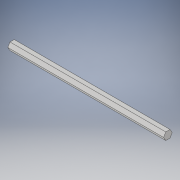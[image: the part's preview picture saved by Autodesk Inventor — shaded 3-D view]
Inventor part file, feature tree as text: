
AUTODESK INVENTOR PART (.ipt)
format: ipt  version: 2018 (Build 220112000, 112)  size: 96,256 bytes
history: native  units: in
note: dims shown in document units (in); Inventor stores cm internally (conversion verified against a paired STEP export)
features: extrude x1, sketch x1
ambient origin geometry x8: Origin, YZ Plane, XZ Plane, XY Plane, X Axis, Y Axis, Z Axis, Center Point
bodies: Solid1 (feature_tree)
feature tree (2):
  extrude  "Extrusion1"  Depth=10.5in TaperAngle=0.0deg
  sketch  "Sketch1"  dims[d0=0.25in d1=10.5in d2=0.0in]
